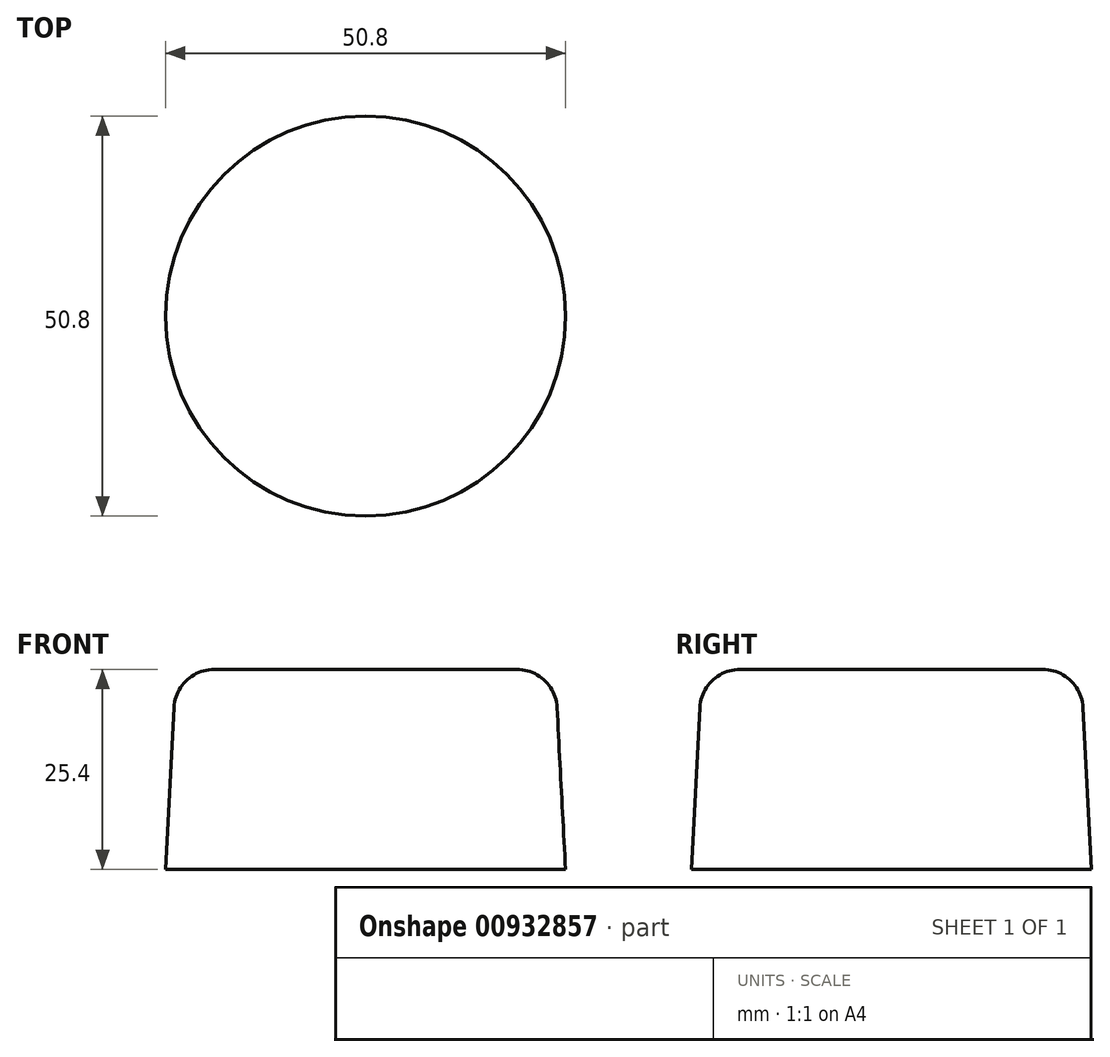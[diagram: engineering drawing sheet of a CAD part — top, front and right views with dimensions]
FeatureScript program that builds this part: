
annotation { "Feature Type Name" : "Feature", "Feature Type Description" : "" }
export const myFeature = defineFeature(function(context is Context, id is Id, definition is map)
    precondition{}
    {
        {
            var Q0;
            Q0=qCreatedBy(makeId("Top.planeOp"),FACE);
            var sketch = newSketch(context, id + "F0", { "sketchPlane" : qUnion([Q0])});
            skCircle(sketch, "E0", {"center": v(0, 0) * mm, "radius": 25.4 * mm});
            skSolve(sketch);
        }
        {
            var Q0;
            Q0=makeQuery(id+"F0.imprint","IMPRINT",FACE,{"disambiguationData":[TD([[makeQuery(id+"F0.imprint","IMPRINT",EDGE,{"derivedFrom":sQuery(id+"F0.wireOp",EDGE,"E0")}),1.0]])]});
            extrude(context, id + "F1", {"entities" : qUnion([Q0]), "surfaceOperationType" : NewSurfaceOperationType.ADD, "depth" : 25.4 * mm, "offsetDistance" : 25.4 * mm, "hasDraft" : true, "draftAngle" : 3 * degree, "draftPullDirection" : true});
        }
        {
            var Q0;
            Q0=makeQuery(id+"F1.opExtrude","CAP_FACE",FACE,{"disambiguationData":[OSD([sQuery(id+"F0.wireOp",EDGE,"E0")])],"isStart":false});
            fillet(context, id + "F2", {"entities" : qUnion([Q0]), "radius" : 5.08 * mm, "tangentPropagation" : true, "allowEdgeOverflow" : false});
        }
    });
